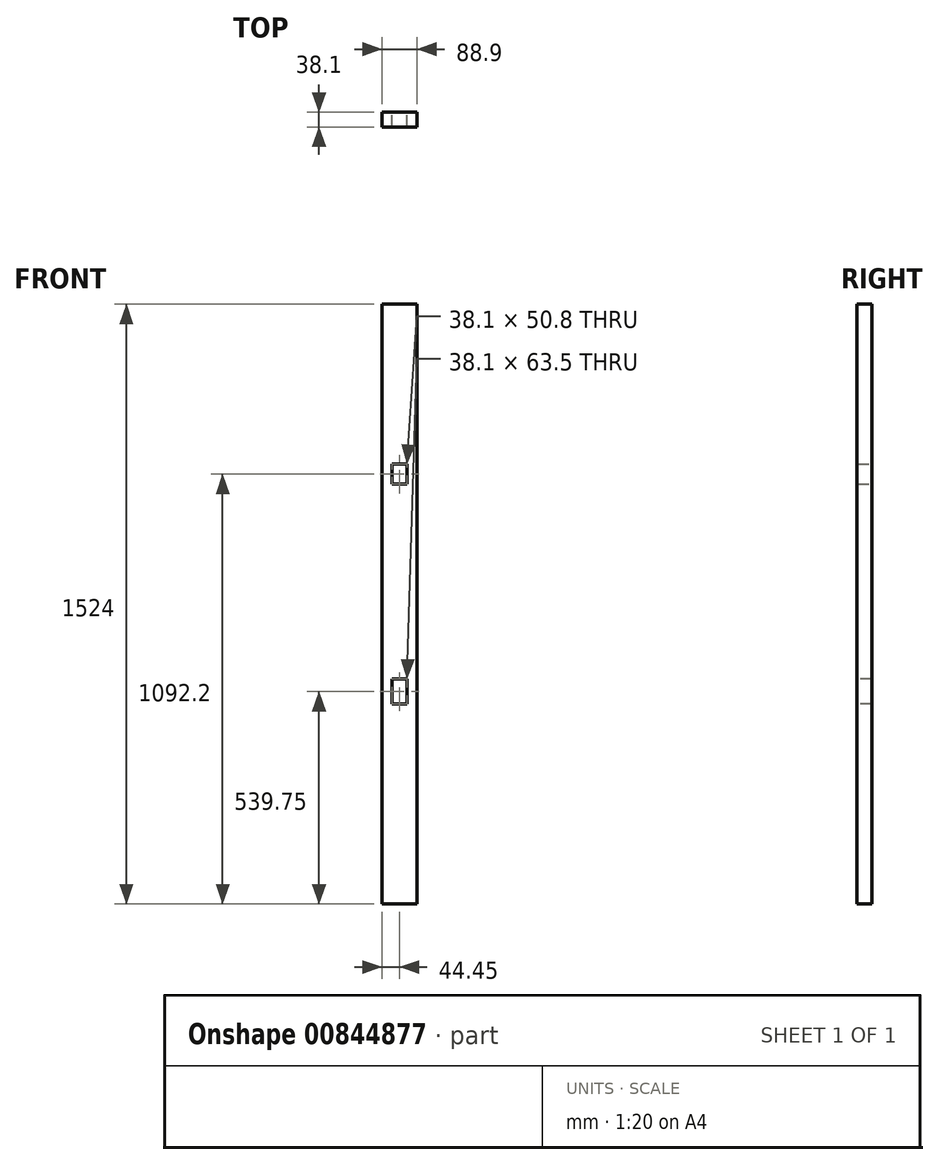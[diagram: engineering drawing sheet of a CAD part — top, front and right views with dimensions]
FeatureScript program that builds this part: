
annotation { "Feature Type Name" : "Feature", "Feature Type Description" : "" }
export const myFeature = defineFeature(function(context is Context, id is Id, definition is map)
    precondition{}
    {
        {
            var Q0;
            Q0=qCreatedBy(makeId("Top.planeOp"),FACE);
            var sketch = newSketch(context, id + "F0", { "sketchPlane" : qUnion([Q0])});
            skLineSegment(sketch, "E0.bottom", {"start": v(0, 0) * mm, "end": v(88.9, 0) * mm});
            skLineSegment(sketch, "E0.top", {"start": v(0, 38.1) * mm, "end": v(88.9, 38.1) * mm});
            skLineSegment(sketch, "E0.left", {"start": v(0, 0) * mm, "end": v(0, 38.1) * mm});
            skLineSegment(sketch, "E0.right", {"start": v(88.9, 0) * mm, "end": v(88.9, 38.1) * mm});
            skSolve(sketch);
        }
        {
            var Q0;
            Q0 = qSketchRegion(id + "F0", true);
            extrude(context, id + "F1", {"entities" : qUnion([Q0]), "depth" : 1524 * mm, "offsetDistance" : 25.4 * mm});
        }
        {
            var Q0;
            Q0=makeQuery(id+"F1.opExtrude","SWEPT_FACE",FACE,{"disambiguationData":[OSD([sQuery(id+"F0.wireOp",EDGE,"E0.top")])]});
            var sketch = newSketch(context, id + "F2", { "sketchPlane" : qUnion([Q0])});
            skLineSegment(sketch, "E1.bottom", {"start": v(-63.5, 1117.6) * mm, "end": v(-25.4, 1117.6) * mm});
            skLineSegment(sketch, "E1.top", {"start": v(-63.5, 1066.8) * mm, "end": v(-25.4, 1066.8) * mm});
            skLineSegment(sketch, "E1.left", {"start": v(-63.5, 1117.6) * mm, "end": v(-63.5, 1066.8) * mm});
            skLineSegment(sketch, "E1.right", {"start": v(-25.4, 1117.6) * mm, "end": v(-25.4, 1066.8) * mm});
            skSolve(sketch);
        }
        {
            var Q0;
            Q0=makeQuery(id+"F2.imprint","IMPRINT",FACE,{"disambiguationData":[TD([[makeQuery(id+"F2.imprint","IMPRINT",EDGE,{"derivedFrom":sQuery(id+"F2.wireOp",EDGE,"E1.bottom")}),-1.0]])]});
            extrude(context, id + "F3", {"entities" : qUnion([Q0]), "operationType" : NewBodyOperationType.REMOVE, "endBound" : BoundingType.UP_TO_NEXT, "oppositeDirection" : true, "depth" : 25.4 * mm, "offsetDistance" : 25.4 * mm});
        }
        {
            var Q0;
            Q0=makeQuery(id+"F1.opExtrude","SWEPT_FACE",FACE,{"disambiguationData":[OSD([sQuery(id+"F0.wireOp",EDGE,"E0.bottom")])]});
            var sketch = newSketch(context, id + "F4", { "sketchPlane" : qUnion([Q0])});
            skLineSegment(sketch, "E2.bottom", {"start": v(25.4, 571.5) * mm, "end": v(63.5, 571.5) * mm});
            skLineSegment(sketch, "E2.top", {"start": v(25.4, 508) * mm, "end": v(63.5, 508) * mm});
            skLineSegment(sketch, "E2.left", {"start": v(25.4, 571.5) * mm, "end": v(25.4, 508) * mm});
            skLineSegment(sketch, "E2.right", {"start": v(63.5, 571.5) * mm, "end": v(63.5, 508) * mm});
            skSolve(sketch);
        }
        {
            var Q0;
            Q0=makeQuery(id+"F4.imprint","IMPRINT",FACE,{"disambiguationData":[TD([[makeQuery(id+"F4.imprint","IMPRINT",EDGE,{"derivedFrom":sQuery(id+"F4.wireOp",EDGE,"E2.bottom")}),-1.0]])]});
            extrude(context, id + "F5", {"entities" : qUnion([Q0]), "operationType" : NewBodyOperationType.REMOVE, "endBound" : BoundingType.UP_TO_NEXT, "oppositeDirection" : true, "depth" : 25.4 * mm, "offsetDistance" : 25.4 * mm});
        }
    });
